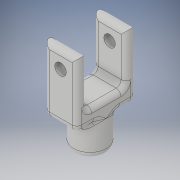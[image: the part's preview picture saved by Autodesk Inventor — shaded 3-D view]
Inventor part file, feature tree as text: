
AUTODESK INVENTOR PART (.ipt)
format: ipt  version: 2019.4 (Build 234330000, 330)  size: 347,648 bytes
history: native  units: mm
features: fillet x5, extrude x4, sketch x4
ambient origin geometry x8: Origin, YZ Plane, XZ Plane, XY Plane, X Axis, Y Axis, Z Axis, Center Point
bodies: Solid1 (feature_tree)
feature tree (13):
  extrude  "Extrusion1"  Depth=10.0mm
  extrude  "Extrusion2"  Depth=10.0mm
  extrude  "Extrusion3"  Depth=10.0mm
  extrude  "Extrusion4"  Depth=1.5mm TaperAngle=0.0deg
  fillet  "Fillet2"  Radius=10.0mm
  fillet  "Fillet4"  Radius=3.0mm
  fillet  "Fillet5"  Radius=10.0mm
  fillet  "Fillet6"  Radius=3.0mm
  fillet  "Fillet7"  Radius=15.0mm
  sketch  "Sketch1"  dims[d0=10.0mm d1=5.0mm]
  sketch  "Sketch2"  dims[d2=10.0mm d3=0.0mm d4=10.0mm]
  sketch  "Sketch3"  dims[d5=15.0mm d6=10.0mm]
  sketch  "Sketch4"  dims[d7=18.0mm d8=5.0mm d9=0.0mm d10=10.0mm d11=3.0mm d12=10.0mm d13=3.0mm d14=15.0mm d15=0.0mm d16=5.0mm d17=3.5mm d18=20.0mm d19=0.0mm d21=2.0mm d23=2.0mm d24=1.5mm d25=1.5mm d26=1.5mm]
